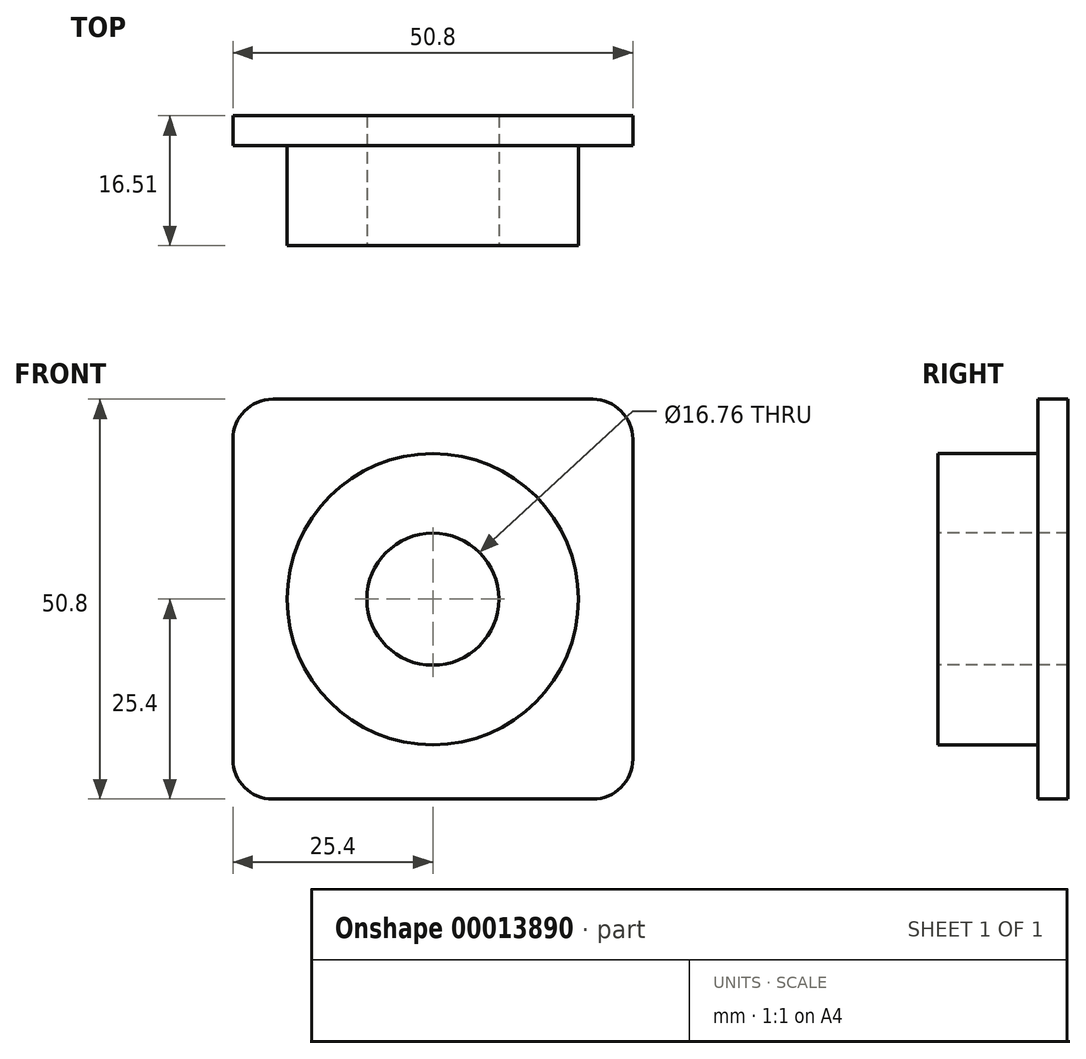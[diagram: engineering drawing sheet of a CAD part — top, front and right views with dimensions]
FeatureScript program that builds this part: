
annotation { "Feature Type Name" : "Feature", "Feature Type Description" : "" }
export const myFeature = defineFeature(function(context is Context, id is Id, definition is map)
    precondition{}
    {
        {
            var Q0;
            Q0=qCreatedBy(makeId("Front.planeOp"),FACE);
            var sketch = newSketch(context, id + "F0", { "sketchPlane" : qUnion([Q0])});
            skCircle(sketch, "E0", {"center": v(0, 0) * mm, "radius": 18.5 * mm});
            skSolve(sketch);
        }
        {
            var Q0;
            Q0 = qSketchRegion(id + "F0", true);
            extrude(context, id + "F1", {"entities" : qUnion([Q0]), "depth" : 12.7 * mm});
        }
        {
            var Q0;
            Q0=makeQuery(id+"F1.opExtrude","CAP_FACE",FACE,{"disambiguationData":[OSD([sQuery(id+"F0.wireOp",EDGE,"E0")])],"isStart":false});
            var sketch = newSketch(context, id + "F2", { "sketchPlane" : qUnion([Q0])});
            skCircle(sketch, "E1", {"center": v(0, 0) * mm, "radius": 8.38 * mm});
            skSolve(sketch);
        }
        {
            var Q0;
            Q0=makeQuery(id+"F1.opExtrude","CAP_FACE",FACE,{"disambiguationData":[OSD([sQuery(id+"F0.wireOp",EDGE,"E0")])],"isStart":true});
            var sketch = newSketch(context, id + "F3", { "sketchPlane" : qUnion([Q0])});
            skLineSegment(sketch, "E2.bottom", {"start": v(25.4, 25.4) * mm, "end": v(-25.4, 25.4) * mm});
            skLineSegment(sketch, "E2.top", {"start": v(25.4, -25.4) * mm, "end": v(-25.4, -25.4) * mm});
            skLineSegment(sketch, "E2.left", {"start": v(25.4, 25.4) * mm, "end": v(25.4, -25.4) * mm});
            skLineSegment(sketch, "E2.right", {"start": v(-25.4, 25.4) * mm, "end": v(-25.4, -25.4) * mm});
            skSolve(sketch);
        }
        {
            var Q0;
            Q0 = qSketchRegion(id + "F3", true);
            extrude(context, id + "F4", {"entities" : qUnion([Q0]), "operationType" : NewBodyOperationType.ADD, "depth" : 3.8 * mm});
        }
        {
            var Q0;
            Q0=makeQuery(id+"F4.opExtrude","SWEPT_EDGE",EDGE,{"disambiguationData":[OSD([sQuery(id+"F3.wireOp",EDGE,"E2.bottom"),sQuery(id+"F3.wireOp",EDGE,"E2.right")])]});
            var Q1;
            Q1=makeQuery(id+"F4.opExtrude","SWEPT_EDGE",EDGE,{"disambiguationData":[OSD([sQuery(id+"F3.wireOp",EDGE,"E2.top"),sQuery(id+"F3.wireOp",EDGE,"E2.right")])]});
            var Q2;
            Q2=makeQuery(id+"F4.opExtrude","SWEPT_EDGE",EDGE,{"disambiguationData":[OSD([sQuery(id+"F3.wireOp",EDGE,"E2.top"),sQuery(id+"F3.wireOp",EDGE,"E2.left")])]});
            var Q3;
            Q3=makeQuery(id+"F4.opExtrude","SWEPT_EDGE",EDGE,{"disambiguationData":[OSD([sQuery(id+"F3.wireOp",EDGE,"E2.bottom"),sQuery(id+"F3.wireOp",EDGE,"E2.left")])]});
            fillet(context, id + "F5", {"entities" : qUnion([Q0, Q1, Q2, Q3]), "radius" : 5.08 * mm, "tangentPropagation" : true, "allowEdgeOverflow" : false});
        }
        {
            var Q0;
            Q0 = qSketchRegion(id + "F2", true);
            extrude(context, id + "F6", {"entities" : qUnion([Q0]), "operationType" : NewBodyOperationType.REMOVE, "oppositeDirection" : true, "depth" : 25.4 * mm});
        }
    });
